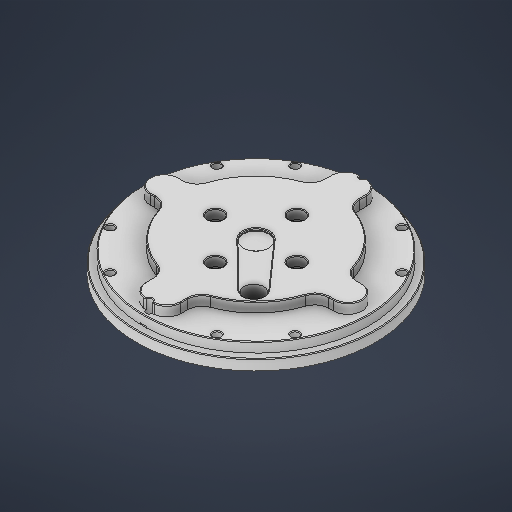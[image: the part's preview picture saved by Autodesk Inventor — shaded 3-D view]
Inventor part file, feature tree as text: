
AUTODESK INVENTOR PART (.ipt)
format: ipt  version: 2025 (Build 290162000, 162)  size: 668,160 bytes
history: native  units: in
note: dims shown in document units (in); Inventor stores cm internally (conversion verified against a paired STEP export)
features: sketch x18, extrude x12, hole x4, chamfer x4
ambient origin geometry x8: Origin, YZ Plane, XZ Plane, XY Plane, X Axis, Y Axis, Z Axis, Center Point
bodies: Solid1 (feature_tree)
feature tree (38):
  sketch  "Sketch1"  dims[d3=4.3307in d24=6.6929in]
  extrude  "Extrusion1"  Depth=6.6929in
  extrude  "Extrusion2"  Depth=5.9843in
  extrude  "Extrusion3"  Depth=4.3307in
  sketch  "Sketch2"  dims[d27=0.9843in d28=4.3307in]
  extrude  "Extrusion4"  Depth=0.3937in
  hole  "Hole1"  [1 undecoded]
  hole  "Hole2"  [1 undecoded]
  sketch  "Sketch4"  dims[d38=0.2953in d39=0.0in d40=2.2835in]
  extrude  "Extrusion5"  Depth=2.2835in
  extrude  "Extrusion6"  Depth=0.1969in
  hole  "Hole3"  [1 undecoded]
  chamfer  "Chamfer1"  Distance=0.7874in Angle=360.0deg
  chamfer  "Chamfer2"  Distance=0.0591in
  hole  "Hole5"  [1 undecoded]
  sketch  "Sketch9"  dims[d69=3.1496in]
  extrude  "Extrusion9"  Depth=0.3937in TaperAngle=45.0deg
  extrude  "Extrusion10"  Depth=0.3937in TaperAngle=45.0deg
  chamfer  "Chamfer4"  Distance=3.7402in
  sketch  "Sketch11"  dims[d74=0.4724in d75=0.0in d76=0.1969in]
  extrude  "Extrusion11"  Depth=0.3937in
  extrude  "Extrusion12"  Depth=0.3937in TaperAngle=360.0deg
  extrude  "Extrusion13"  Depth=0.3937in
  extrude  "Extrusion15"  Depth=0.3937in
  chamfer  "Chamfer6"  Distance=0.7185in
  sketch  "Sketch Circular Pattern1"  dims[d25=6.2992in d26=5.9843in]
  sketch  "Sketch3"  dims[d31=0.3937in d32=0.3937in]
  sketch  "Sketch Circular Pattern2"  dims[d29=0.7874in d30=0.3937in]
  sketch  "Sketch5"  dims[d41=0.4331in d42=0.1969in]
  sketch  "Sketch Circular Pattern3"  dims[d34=0.8465in d35=0.0in d36=0.5709in d37=0.0in]
  sketch  "Sketch7"  dims[d56=5.9843in]
  sketch  "Sketch Circular Pattern5"  dims[d43=1.5748in d45=360.0deg d47=0.2657in d48=0.0in]
  sketch  "Sketch Circular Pattern6"  dims[d49=0.2165in d50=0.7874in d51=0.1575in d52=0.0787in d53=90.0deg d54=0.315in d55=0.8108in]
  sketch  "Sketch10"  dims[d71=0.7874in d72=0.0591in d73=0.0in]
  sketch  "Sketch Circular Pattern7"  dims[d57=0.1378in d58=0.7874in d60=360.0deg]
  sketch  "Sketch Circular Pattern8"  dims[d62=0.1772in d63=0.315in d64=0.1575in d65=0.0787in d66=90.0deg d67=0.4646in d68=0.8108in]
  sketch  "Sketch Circular Pattern9"  dims[d70=0.1969in]
  sketch  "Sketch12"  dims[d77=4.7244in d79=360.0deg d81=0.2165in d82=0.3937in d83=0.1575in d84=0.0787in d85=90.0deg d86=0.3937in d87=0.8108in d88=0.0197in d89=0.0787in d90=45.0deg d91=0.0197in d92=0.0787in d93=45.0deg d107=3.7402in d108=0.1969in d109=6.2992in d111=360.0deg d113=0.1969in d114=0.7874in d115=0.748in d116=0.3543in d117=90.0deg d118=0.7874in d119=0.8108in d139=0.7185in d140=3.1496in d141=0.7185in d142=3.1496in d144=360.0deg d146=0.0689in d147=0.0in d151=0.5512in d152=1.7717in d153=0.0in d154=0.0in d155=0.0197in d156=0.0787in d157=45.0deg d158=0.5512in d159=1.7717in d160=0.3346in d161=4.7244in d163=360.0deg d165=0.3002in d166=0.7874in d168=360.0deg d170=0.3159in d171=1.5748in d173=360.0deg d175=0.1673in d176=0.0in d177=0.3248in d178=0.0in d179=0.1673in d180=0.0in d181=1.7717in d187=0.3117in d188=0.0492in d189=0.0in d190=0.0197in d191=0.0787in d192=45.0deg d137=0.0197in d138=0.0344in]
note: 4 required parameter values undecoded (feature->parameter linkage not recoverable at this tier; creation-order binding heuristic only, values carry confidence <= 0.55)
